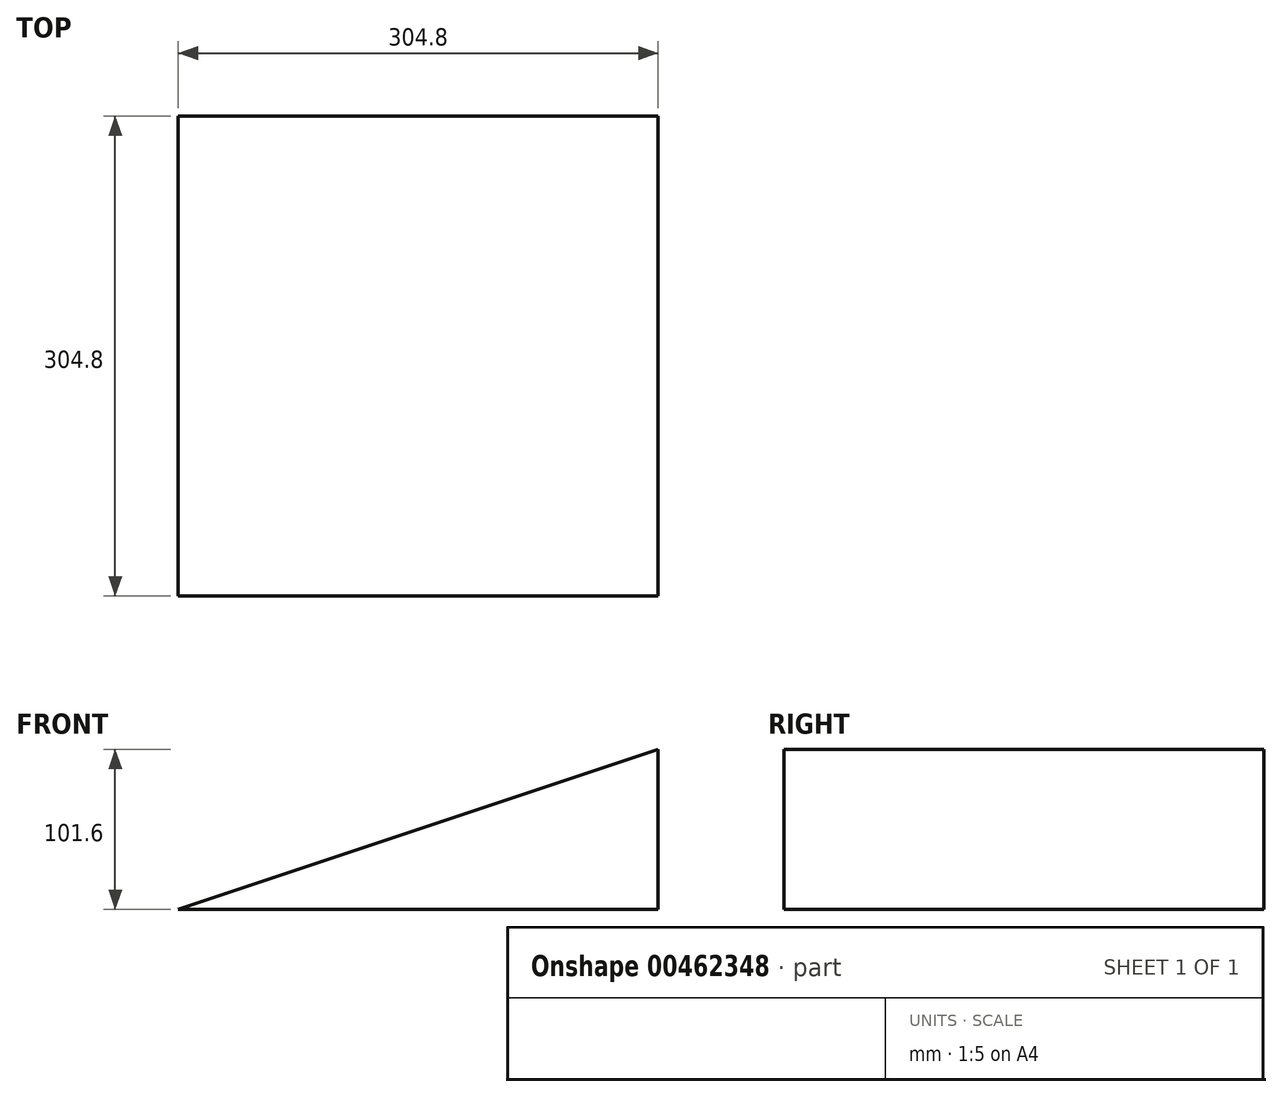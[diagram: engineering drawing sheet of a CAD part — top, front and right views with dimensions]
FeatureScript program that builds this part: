
annotation { "Feature Type Name" : "Feature", "Feature Type Description" : "" }
export const myFeature = defineFeature(function(context is Context, id is Id, definition is map)
    precondition{}
    {
        {
            var Q0;
            Q0=qCreatedBy(makeId("Front.planeOp"),FACE);
            var sketch = newSketch(context, id + "F0", { "sketchPlane" : qUnion([Q0])});
            skLineSegment(sketch, "E0", {"start": v(0, 0) * mm, "end": v(304.8, 101.6) * mm});
            skLineSegment(sketch, "E1", {"start": v(0, 0) * mm, "end": v(304.8, 0) * mm});
            skLineSegment(sketch, "E2", {"start": v(304.8, 0) * mm, "end": v(304.8, 101.6) * mm});
            skSolve(sketch);
        }
        {
            var Q0;
            Q0=makeQuery(id+"F0.imprint","IMPRINT",FACE,{"disambiguationData":[TD([[makeQuery(id+"F0.imprint","IMPRINT",EDGE,{"derivedFrom":sQuery(id+"F0.wireOp",EDGE,"E0")}),-1.0]])]});
            extrude(context, id + "F1", {"entities" : qUnion([Q0]), "depth" : 304.8 * mm});
        }
    });
